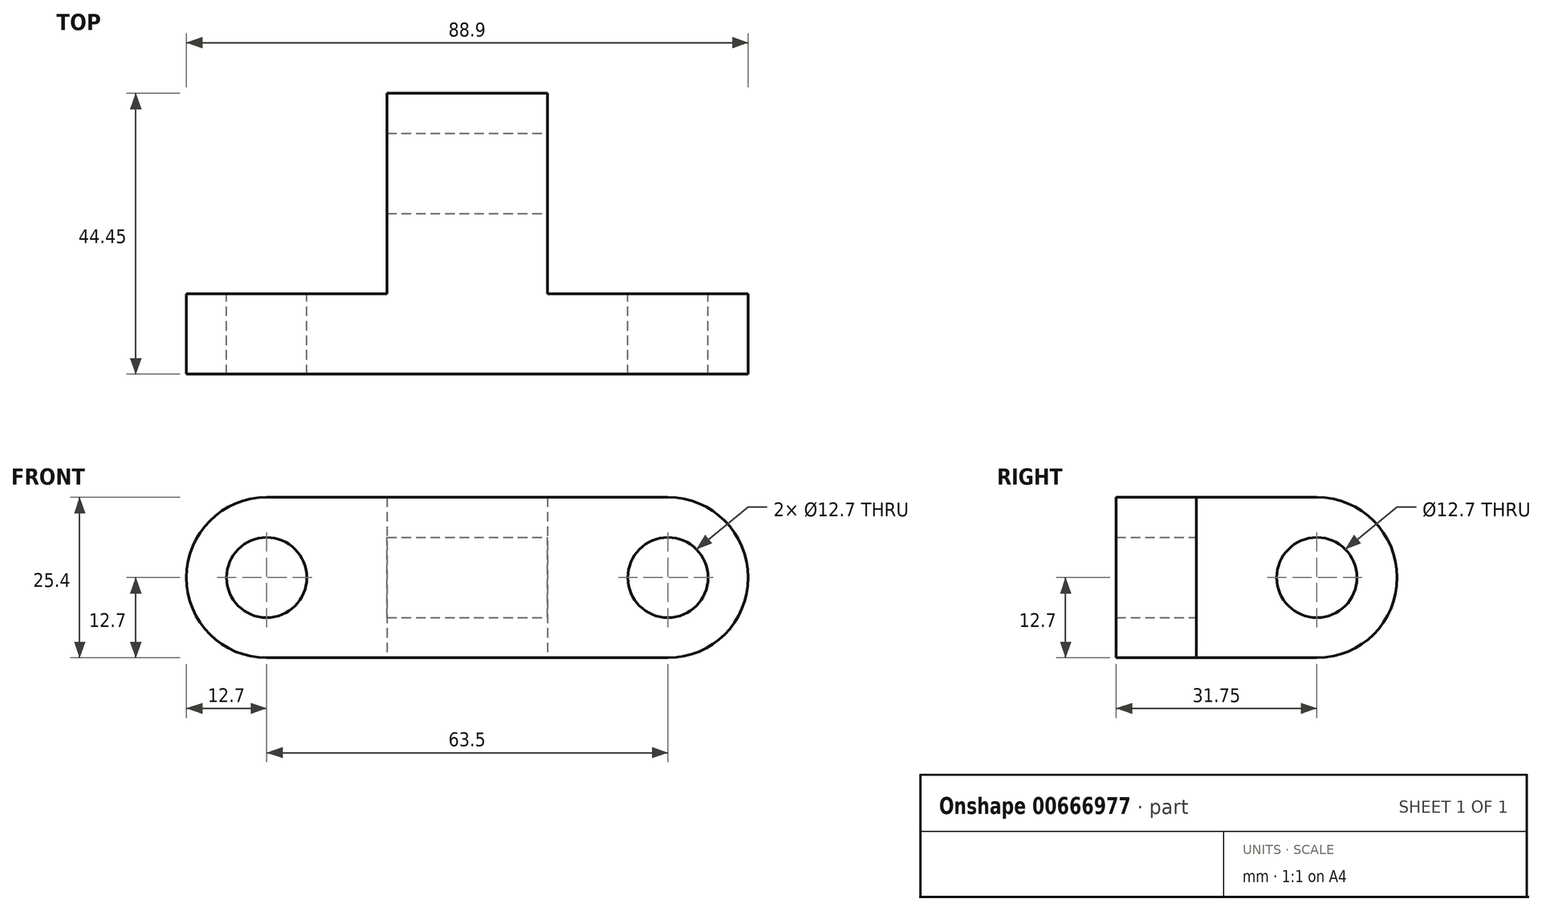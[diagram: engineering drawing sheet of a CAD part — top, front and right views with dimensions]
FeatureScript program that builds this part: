
annotation { "Feature Type Name" : "Feature", "Feature Type Description" : "" }
export const myFeature = defineFeature(function(context is Context, id is Id, definition is map)
    precondition{}
    {
        {
            var Q0;
            Q0=qCreatedBy(makeId("Top.planeOp"),FACE);
            var sketch = newSketch(context, id + "F0", { "sketchPlane" : qUnion([Q0])});
            skLineSegment(sketch, "E0", {"start": v(0, 0) * mm, "end": v(25.4, 0) * mm});
            skLineSegment(sketch, "E1", {"start": v(25.4, 0) * mm, "end": v(25.4, 44.45) * mm});
            skLineSegment(sketch, "E2", {"start": v(0, 0) * mm, "end": v(0, 44.45) * mm});
            skLineSegment(sketch, "E3", {"start": v(25.4, 44.45) * mm, "end": v(0, 44.45) * mm});
            skLineSegment(sketch, "E4", {"start": v(25.4, 0) * mm, "end": v(57.15, 0) * mm});
            skLineSegment(sketch, "E5", {"start": v(57.15, 0) * mm, "end": v(57.15, 12.7) * mm});
            skLineSegment(sketch, "E6", {"start": v(57.15, 12.7) * mm, "end": v(25.4, 12.7) * mm});
            skLineSegment(sketch, "E7", {"start": v(0, 0) * mm, "end": v(-31.75, 0) * mm});
            skLineSegment(sketch, "E8", {"start": v(-31.75, 0) * mm, "end": v(-31.75, 12.7) * mm});
            skLineSegment(sketch, "E9", {"start": v(-31.75, 12.7) * mm, "end": v(0, 12.7) * mm});
            skSolve(sketch);
        }
        {
            var Q0;
            Q0 = qSketchRegion(id + "F0", true);
            extrude(context, id + "F1", {"entities" : qUnion([Q0]), "depth" : 25.4 * mm, "offsetDistance" : 25.4 * mm});
        }
        {
            var Q0;
            Q0=makeQuery(id+"F1.opExtrude","SWEPT_FACE",FACE,{"disambiguationData":[OSD([sQuery(id+"F0.wireOp",EDGE,"E1")])]});
            var sketch = newSketch(context, id + "F2", { "sketchPlane" : qUnion([Q0])});
            skLineSegment(sketch, "E10", {"start": v(12.7, 25.4) * mm, "end": v(31.75, 25.4) * mm});
            skLineSegment(sketch, "E11", {"start": v(31.75, 25.4) * mm, "end": v(31.75, 12.7) * mm});
            skCircle(sketch, "E12", {"center": v(31.75, 12.7) * mm, "radius": 6.35 * mm});
            skSolve(sketch);
        }
        {
            var Q0;
            Q0=makeQuery(id+"F2.imprint","IMPRINT",FACE,{"disambiguationData":[TD([[makeQuery(id+"F2.imprint","IMPRINT",EDGE,{"derivedFrom":sQuery(id+"F2.wireOp",EDGE,"E12")}),1.0]])]});
            extrude(context, id + "F3", {"entities" : qUnion([Q0]), "operationType" : NewBodyOperationType.REMOVE, "oppositeDirection" : true, "depth" : 25.4 * mm, "offsetDistance" : 25.4 * mm});
        }
        {
            var Q0;
            Q0=makeQuery(id+"F1.opExtrude","SWEPT_FACE",FACE,{"disambiguationData":[OSD([sQuery(id+"F0.wireOp",EDGE,"E6")])]});
            var sketch = newSketch(context, id + "F4", { "sketchPlane" : qUnion([Q0])});
            skLineSegment(sketch, "E13", {"start": v(-25.4, 25.4) * mm, "end": v(-44.45, 25.4) * mm});
            skLineSegment(sketch, "E14", {"start": v(-44.45, 25.4) * mm, "end": v(-44.45, 12.7) * mm});
            skCircle(sketch, "E15", {"center": v(-44.45, 12.7) * mm, "radius": 6.35 * mm});
            skSolve(sketch);
        }
        {
            var Q0;
            Q0 = qSketchRegion(id + "F4", true);
            extrude(context, id + "F5", {"entities" : qUnion([Q0]), "operationType" : NewBodyOperationType.REMOVE, "oppositeDirection" : true, "depth" : 25.4 * mm, "offsetDistance" : 25.4 * mm});
        }
        {
            var Q0;
            Q0=makeQuery(id+"F1.opExtrude","SWEPT_FACE",FACE,{"disambiguationData":[OSD([sQuery(id+"F0.wireOp",EDGE,"E9")])]});
            var sketch = newSketch(context, id + "F6", { "sketchPlane" : qUnion([Q0])});
            skLineSegment(sketch, "E16", {"start": v(0, 0) * mm, "end": v(19.05, 0) * mm});
            skLineSegment(sketch, "E17", {"start": v(19.05, 0) * mm, "end": v(19.05, 12.7) * mm});
            skCircle(sketch, "E18", {"center": v(19.05, 12.7) * mm, "radius": 6.35 * mm});
            skSolve(sketch);
        }
        {
            var Q0;
            Q0 = qSketchRegion(id + "F6", true);
            extrude(context, id + "F7", {"entities" : qUnion([Q0]), "operationType" : NewBodyOperationType.REMOVE, "oppositeDirection" : true, "depth" : 25.4 * mm, "offsetDistance" : 25.4 * mm});
        }
        {
            var Q0;
            Q0=makeQuery(id+"F1.opExtrude","CAP_EDGE",EDGE,{"disambiguationData":[OSD([sQuery(id+"F0.wireOp",EDGE,"E5")])],"isStart":false});
            var Q1;
            Q1=makeQuery(id+"F1.opExtrude","CAP_EDGE",EDGE,{"disambiguationData":[OSD([sQuery(id+"F0.wireOp",EDGE,"E5")])],"isStart":true});
            var Q2;
            Q2=makeQuery(id+"F1.opExtrude","CAP_EDGE",EDGE,{"disambiguationData":[OSD([sQuery(id+"F0.wireOp",EDGE,"E3")])],"isStart":false});
            var Q3;
            Q3=makeQuery(id+"F1.opExtrude","CAP_EDGE",EDGE,{"disambiguationData":[OSD([sQuery(id+"F0.wireOp",EDGE,"E3")])],"isStart":true});
            var Q4;
            Q4=makeQuery(id+"F1.opExtrude","CAP_EDGE",EDGE,{"disambiguationData":[OSD([sQuery(id+"F0.wireOp",EDGE,"E8")])],"isStart":true});
            var Q5;
            Q5=makeQuery(id+"F1.opExtrude","CAP_EDGE",EDGE,{"disambiguationData":[OSD([sQuery(id+"F0.wireOp",EDGE,"E8")])],"isStart":false});
            fillet(context, id + "F8", {"entities" : qUnion([Q0, Q1, Q2, Q3, Q4, Q5]), "radius" : 12.7 * mm, "tangentPropagation" : true, "allowEdgeOverflow" : false});
        }
    });
